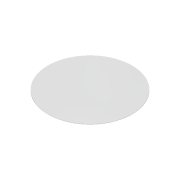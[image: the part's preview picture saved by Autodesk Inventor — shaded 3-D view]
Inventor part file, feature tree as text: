
AUTODESK INVENTOR PART (.ipt)
format: ipt  version: 2019 (Build 230136000, 136)  size: 73,728 bytes
history: native  units: mm
features: extrude x1, sketch x1
ambient origin geometry x8: Origin, YZ Plane, XZ Plane, XY Plane, X Axis, Y Axis, Z Axis, Center Point
bodies: Volumenkörper1 (feature_tree)
feature tree (2):
  extrude  "Extrusion1"  Depth=0.15mm TaperAngle=0.0deg
  sketch  "Skizze1"  dims[d0=25.0mm d1=0.15mm d2=0.0mm]
